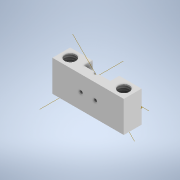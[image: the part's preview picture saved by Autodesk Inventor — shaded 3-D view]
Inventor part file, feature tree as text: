
AUTODESK INVENTOR PART (.ipt)
format: ipt  version: 2021.2 (Build 252289000, 289)  size: 181,248 bytes
history: native  units: in
note: dims shown in document units (in); Inventor stores cm internally (conversion verified against a paired STEP export)
features: hole x7, sketch x6, other x6, extrude x1
ambient origin geometry x8: Origin, YZ Plane, XZ Plane, XY Plane, X Axis, Y Axis, Z Axis, Center Point
bodies: Solid1 (feature_tree)
feature tree (20):
  extrude  "Extrusion1"  Depth=0.25in
  sketch  "Sketch2"  dims[d2=0.375in d3=0.4375in d4=0.0in]
  other  "Work Axis1"
  other  "Work Point1"
  hole  "Hole1"  [1 undecoded]
  other  "Work Axis3"
  other  "Work Point2"
  hole  "Hole3"  [1 undecoded]
  hole  "Hole2"  [1 undecoded]
  hole  "Hole4"  [1 undecoded]
  hole  "Hole5"  [1 undecoded]
  other  "Work Point3"
  other  "Work Axis5"
  hole  "Hole6"  [1 undecoded]
  hole  "Hole7"  [1 undecoded]
  sketch  "Sketch1"  dims[d0=1.0in d1=0.25in]
  sketch  "Sketch6"  dims[d5=0.125in d6=0.125in]
  sketch  "Sketch7"  dims[d60=1.0in d61=1.0in d13=0.05in d14=0.75in d15=0.375in d16=0.25in d17=0.5635in d18=0.1in d19=0.0in]
  sketch  "Sketch8"  dims[d22=0.156in d23=0.2in d24=0.119in d25=0.25in d26=0.5635in d27=0.25in d28=0.0in]
  sketch  "Sketch9"  dims[d62=1.0in d63=1.0in d33=0.05in d34=0.05in d35=0.119in d36=0.25in d37=0.5635in d38=0.1in d39=0.0in d42=0.15in d43=0.05in d44=0.05in d45=0.119in d46=0.25in d47=0.5635in d48=0.145in d49=0.0in d52=0.15in d53=0.05in d54=0.05in d55=0.119in d56=0.25in d57=0.5635in d58=0.145in d59=0.0in d64=0.4in d65=0.4in d66=0.0465in d67=0.12in d68=0.119in d69=0.25in d70=0.5635in d71=0.183in d72=0.0in d73=0.5in d74=0.05in d75=0.11in d76=0.119in d77=0.25in d78=0.5635in d79=0.169in d80=0.0in d81=0.0075in d50=1.0in d51=1.0in]
note: 7 required parameter values undecoded (feature->parameter linkage not recoverable at this tier; creation-order binding heuristic only, values carry confidence <= 0.55)
